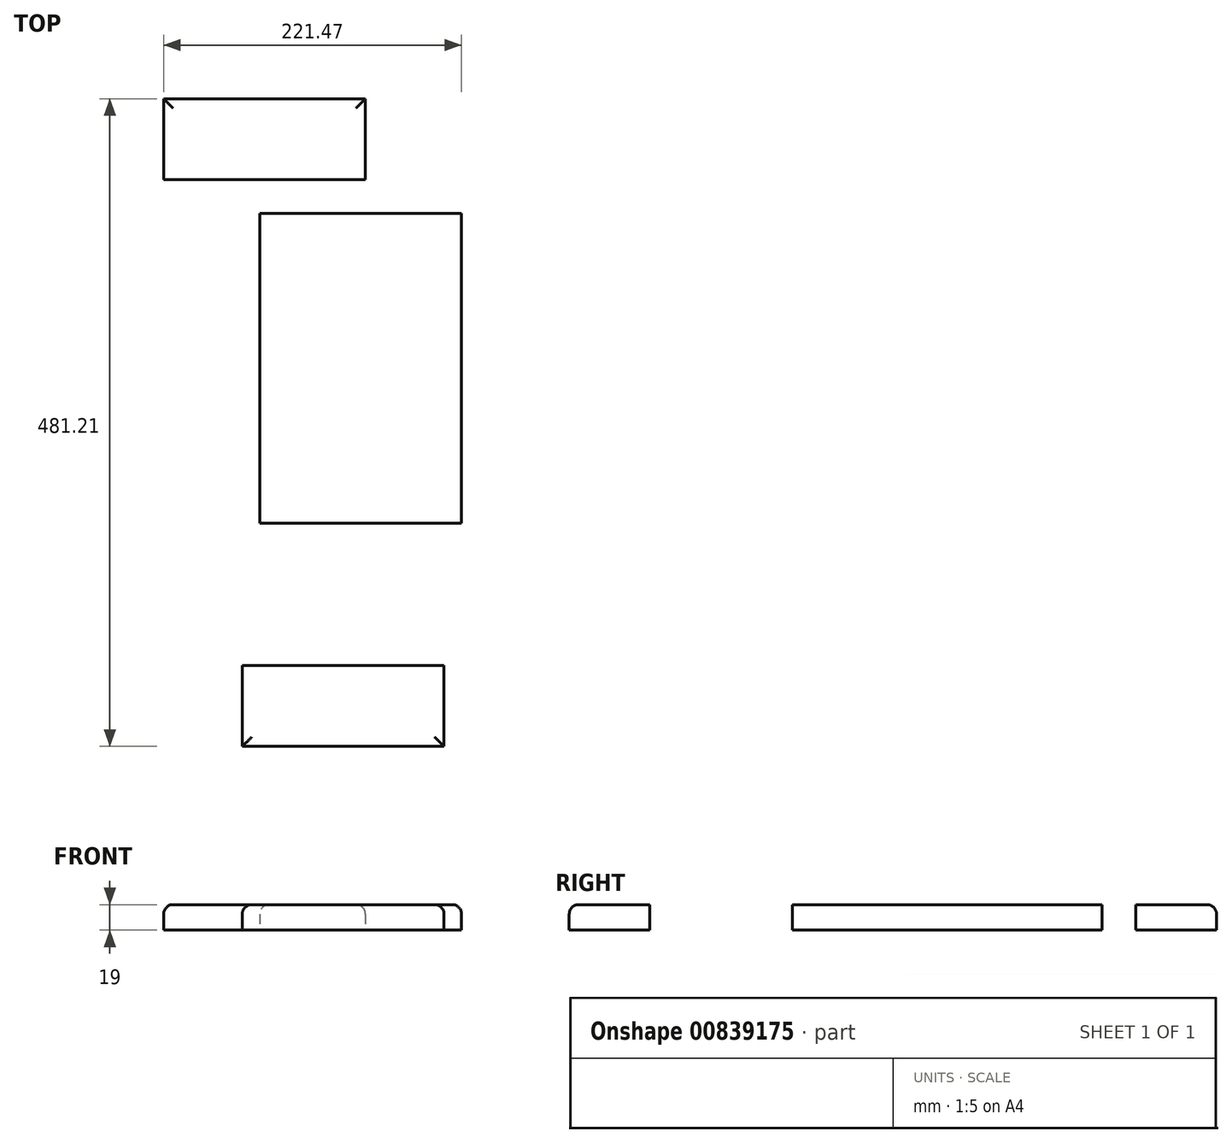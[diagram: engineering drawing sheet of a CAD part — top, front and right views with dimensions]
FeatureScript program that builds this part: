
annotation { "Feature Type Name" : "Feature", "Feature Type Description" : "" }
export const myFeature = defineFeature(function(context is Context, id is Id, definition is map)
    precondition{}
    {
        {
            var Q0;
            Q0=qCreatedBy(makeId("Top.planeOp"),FACE);
            var sketch = newSketch(context, id + "F0", { "sketchPlane" : qUnion([Q0])});
            skLineSegment(sketch, "E0.bottom", {"start": v(-312.87, 85.2) * mm, "end": v(-162.87, 85.2) * mm});
            skLineSegment(sketch, "E0.top", {"start": v(-312.87, 25.2) * mm, "end": v(-162.87, 25.2) * mm});
            skLineSegment(sketch, "E0.left", {"start": v(-312.87, 85.2) * mm, "end": v(-312.87, 25.2) * mm});
            skLineSegment(sketch, "E0.right", {"start": v(-162.87, 85.2) * mm, "end": v(-162.87, 25.2) * mm});
            skSolve(sketch);
        }
        {
            var Q0;
            Q0=qCreatedBy(makeId("Top.planeOp"),FACE);
            var sketch = newSketch(context, id + "F1", { "sketchPlane" : qUnion([Q0])});
            skLineSegment(sketch, "E1.bottom", {"start": v(-241.4, 0) * mm, "end": v(-91.4, 0) * mm});
            skLineSegment(sketch, "E1.top", {"start": v(-241.4, -230) * mm, "end": v(-91.4, -230) * mm});
            skLineSegment(sketch, "E1.left", {"start": v(-241.4, 0) * mm, "end": v(-241.4, -230) * mm});
            skLineSegment(sketch, "E1.right", {"start": v(-91.4, 0) * mm, "end": v(-91.4, -230) * mm});
            skSolve(sketch);
        }
        {
            var Q0;
            Q0=makeQuery(id+"F0.imprint","IMPRINT",FACE,{"disambiguationData":[TD([[makeQuery(id+"F0.imprint","IMPRINT",EDGE,{"derivedFrom":sQuery(id+"F0.wireOp",EDGE,"E0.bottom")}),-1.0]])]});
            extrude(context, id + "F2", {"entities" : qUnion([Q0]), "depth" : 19 * mm, "offsetDistance" : 25 * mm});
        }
        {
            var Q0;
            Q0=makeQuery(id+"F1.imprint","IMPRINT",FACE,{"disambiguationData":[TD([[makeQuery(id+"F1.imprint","IMPRINT",EDGE,{"derivedFrom":sQuery(id+"F1.wireOp",EDGE,"E1.bottom")}),-1.0]])]});
            extrude(context, id + "F3", {"entities" : qUnion([Q0]), "depth" : 19 * mm, "offsetDistance" : 25 * mm});
        }
        {
            var Q0;
            Q0=qCreatedBy(makeId("Top.planeOp"),FACE);
            var sketch = newSketch(context, id + "F4", { "sketchPlane" : qUnion([Q0])});
            skLineSegment(sketch, "E2.bottom", {"start": v(-254.43, -336) * mm, "end": v(-104.43, -336) * mm});
            skLineSegment(sketch, "E2.top", {"start": v(-254.43, -396) * mm, "end": v(-104.43, -396) * mm});
            skLineSegment(sketch, "E2.left", {"start": v(-254.43, -336) * mm, "end": v(-254.43, -396) * mm});
            skLineSegment(sketch, "E2.right", {"start": v(-104.43, -336) * mm, "end": v(-104.43, -396) * mm});
            skSolve(sketch);
        }
        {
            var Q0;
            Q0=makeQuery(id+"F4.imprint","IMPRINT",FACE,{"disambiguationData":[TD([[makeQuery(id+"F4.imprint","IMPRINT",EDGE,{"derivedFrom":sQuery(id+"F4.wireOp",EDGE,"E2.bottom")}),-1.0]])]});
            extrude(context, id + "F5", {"entities" : qUnion([Q0]), "depth" : 19 * mm, "offsetDistance" : 25 * mm});
        }
        {
            var Q0;
            Q0=makeQuery(id+"F5.opExtrude","CAP_EDGE",EDGE,{"disambiguationData":[OSD([sQuery(id+"F4.wireOp",EDGE,"E2.top")])],"isStart":false});
            var Q1;
            Q1=makeQuery(id+"F5.opExtrude","CAP_EDGE",EDGE,{"disambiguationData":[OSD([sQuery(id+"F4.wireOp",EDGE,"E2.right")])],"isStart":false});
            var Q2;
            Q2=makeQuery(id+"F5.opExtrude","CAP_EDGE",EDGE,{"disambiguationData":[OSD([sQuery(id+"F4.wireOp",EDGE,"E2.left")])],"isStart":false});
            var Q3;
            Q3=makeQuery(id+"F3.opExtrude","CAP_EDGE",EDGE,{"disambiguationData":[OSD([sQuery(id+"F1.wireOp",EDGE,"E1.right")])],"isStart":false});
            var Q4;
            Q4=makeQuery(id+"F3.opExtrude","CAP_EDGE",EDGE,{"disambiguationData":[OSD([sQuery(id+"F1.wireOp",EDGE,"E1.left")])],"isStart":false});
            var Q5;
            Q5=makeQuery(id+"F2.opExtrude","CAP_EDGE",EDGE,{"disambiguationData":[OSD([sQuery(id+"F0.wireOp",EDGE,"E0.right")])],"isStart":false});
            var Q6;
            Q6=makeQuery(id+"F2.opExtrude","CAP_EDGE",EDGE,{"disambiguationData":[OSD([sQuery(id+"F0.wireOp",EDGE,"E0.bottom")])],"isStart":false});
            var Q7;
            Q7=makeQuery(id+"F2.opExtrude","CAP_EDGE",EDGE,{"disambiguationData":[OSD([sQuery(id+"F0.wireOp",EDGE,"E0.left")])],"isStart":false});
            fillet(context, id + "F6", {"entities" : qUnion([Q0, Q1, Q2, Q3, Q4, Q5, Q6, Q7]), "radius" : 7 * mm, "tangentPropagation" : true, "allowEdgeOverflow" : false});
        }
    });
